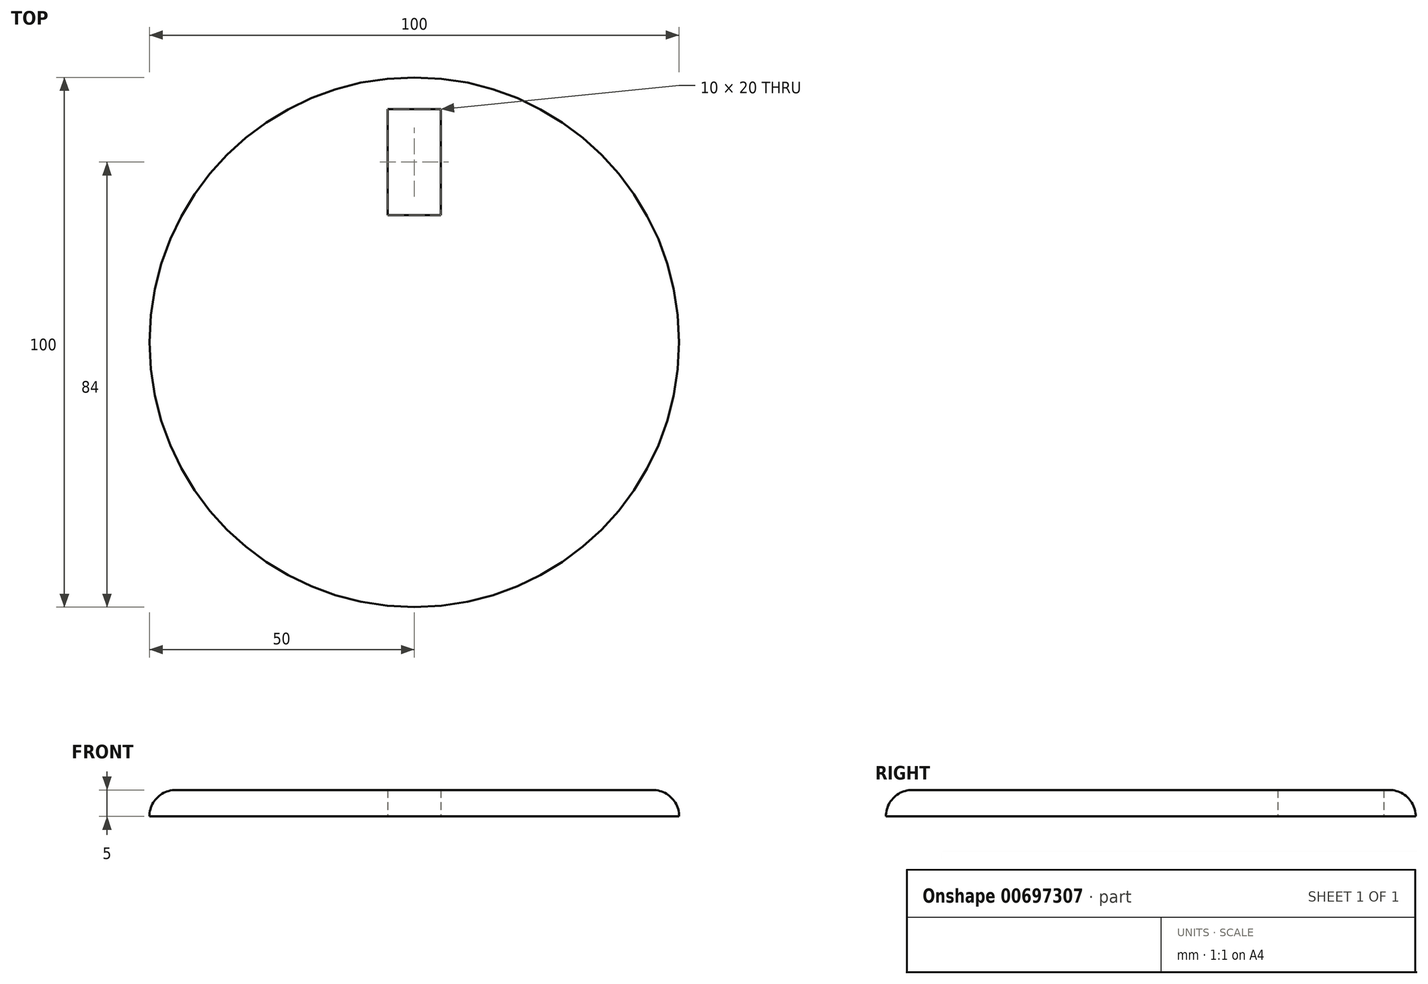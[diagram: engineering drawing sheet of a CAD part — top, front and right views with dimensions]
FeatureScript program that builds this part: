
annotation { "Feature Type Name" : "Feature", "Feature Type Description" : "" }
export const myFeature = defineFeature(function(context is Context, id is Id, definition is map)
    precondition{}
    {
        {
            var Q0;
            Q0=qCreatedBy(makeId("Top.planeOp"),FACE);
            var sketch = newSketch(context, id + "F0", { "sketchPlane" : qUnion([Q0])});
            skCircle(sketch, "E0", {"center": v(0, 0) * mm, "radius": 50 * mm});
            skLineSegment(sketch, "E1.bottom", {"start": v(5, 24) * mm, "end": v(-5, 24) * mm});
            skLineSegment(sketch, "E1.top", {"start": v(5, 44) * mm, "end": v(-5, 44) * mm});
            skLineSegment(sketch, "E1.left", {"start": v(5, 24) * mm, "end": v(5, 44) * mm});
            skLineSegment(sketch, "E1.right", {"start": v(-5, 24) * mm, "end": v(-5, 44) * mm});
            skPoint(sketch, "E1.middle", {"position": v(0, 34) * mm});
            skSolve(sketch);
        }
        {
            var Q0;
            Q0=makeQuery(id+"F0.imprint","IMPRINT",FACE,{"disambiguationData":[TD([[makeQuery(id+"F0.imprint","IMPRINT",EDGE,{"derivedFrom":sQuery(id+"F0.wireOp",EDGE,"E0")}),1.0]])]});
            extrude(context, id + "F1", {"entities" : qUnion([Q0]), "depth" : 5 * mm, "offsetDistance" : 25 * mm});
        }
        {
            var Q0;
            Q0=makeQuery(id+"F1.opExtrude","CAP_EDGE",EDGE,{"disambiguationData":[OSD([sQuery(id+"F0.wireOp",EDGE,"E0")])],"isStart":false});
            fillet(context, id + "F2", {"entities" : qUnion([Q0]), "radius" : 5 * mm, "tangentPropagation" : true, "allowEdgeOverflow" : false});
        }
    });
